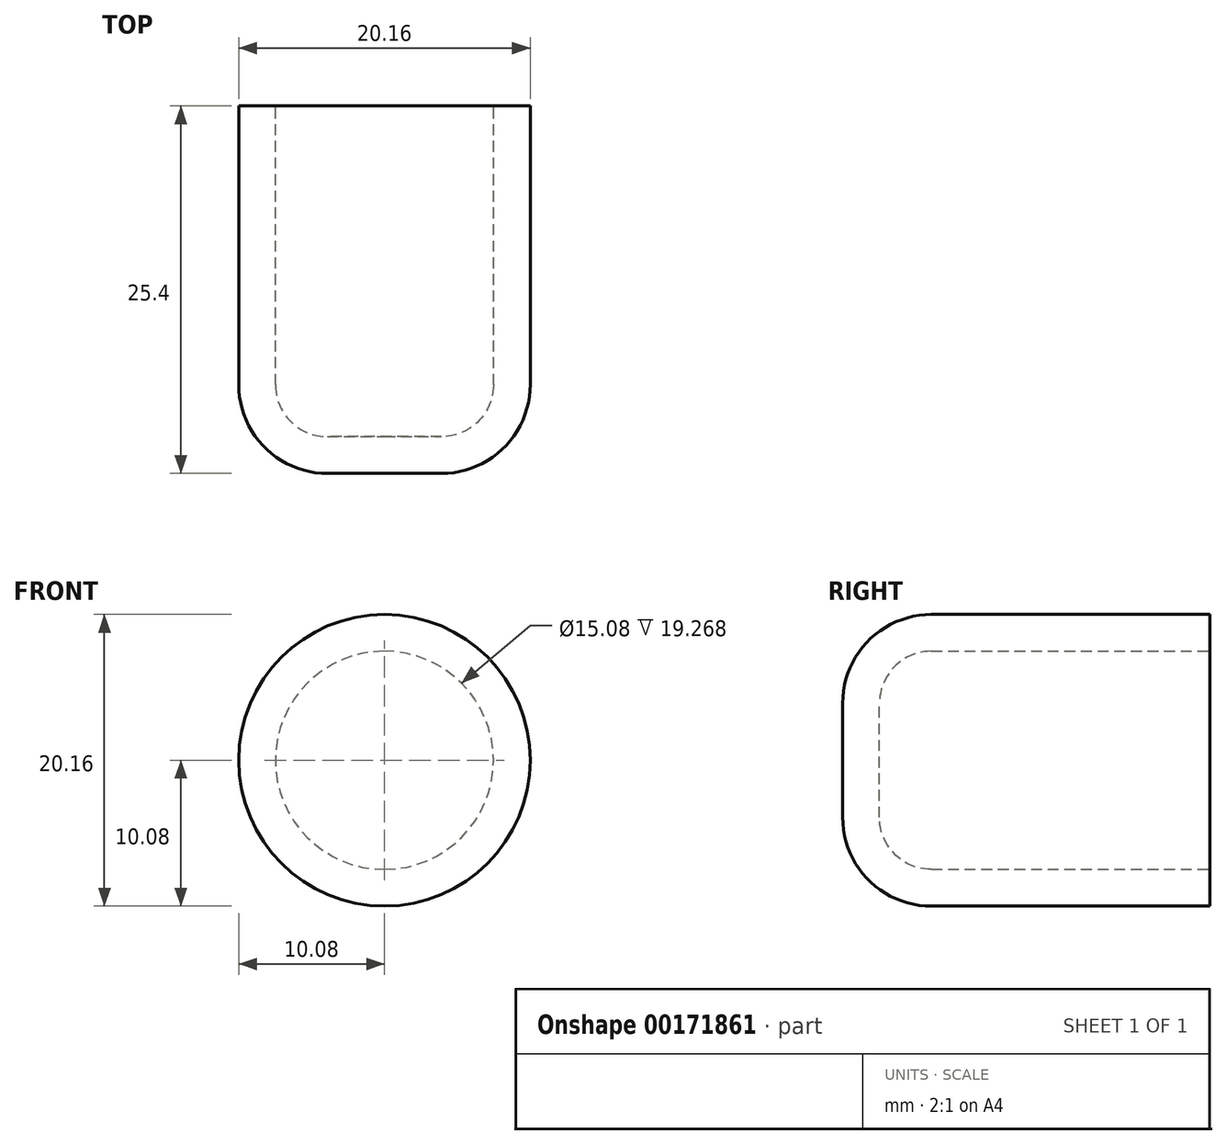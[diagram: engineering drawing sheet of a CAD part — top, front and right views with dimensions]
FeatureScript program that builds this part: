
annotation { "Feature Type Name" : "Feature", "Feature Type Description" : "" }
export const myFeature = defineFeature(function(context is Context, id is Id, definition is map)
    precondition{}
    {
        {
            var Q0;
            Q0=qCreatedBy(makeId("Front.planeOp"),FACE);
            var sketch = newSketch(context, id + "F0", { "sketchPlane" : qUnion([Q0])});
            skCircle(sketch, "E0", {"center": v(0, 0) * mm, "radius": 10.08 * mm});
            skSolve(sketch);
        }
        {
            var Q0;
            Q0 = qSketchRegion(id + "F0", true);
            extrude(context, id + "F1", {"entities" : qUnion([Q0]), "depth" : 25.4 * mm});
        }
        {
            var Q0;
            Q0=makeQuery(id+"F1.opExtrude","CAP_EDGE",EDGE,{"disambiguationData":[OSD([sQuery(id+"F0.wireOp",EDGE,"E0")])],"isStart":false});
            fillet(context, id + "F2", {"entities" : qUnion([Q0]), "radius" : 6.13 * mm, "tangentPropagation" : true, "allowEdgeOverflow" : false});
        }
        {
            var Q0;
            Q0=makeQuery(id+"F1.opExtrude","CAP_FACE",FACE,{"disambiguationData":[OSD([sQuery(id+"F0.wireOp",EDGE,"E0")])],"isStart":true});
            shell(context, id + "F3", {"entities" : qUnion([Q0]), "thickness" : 2.54 * mm});
        }
    });
